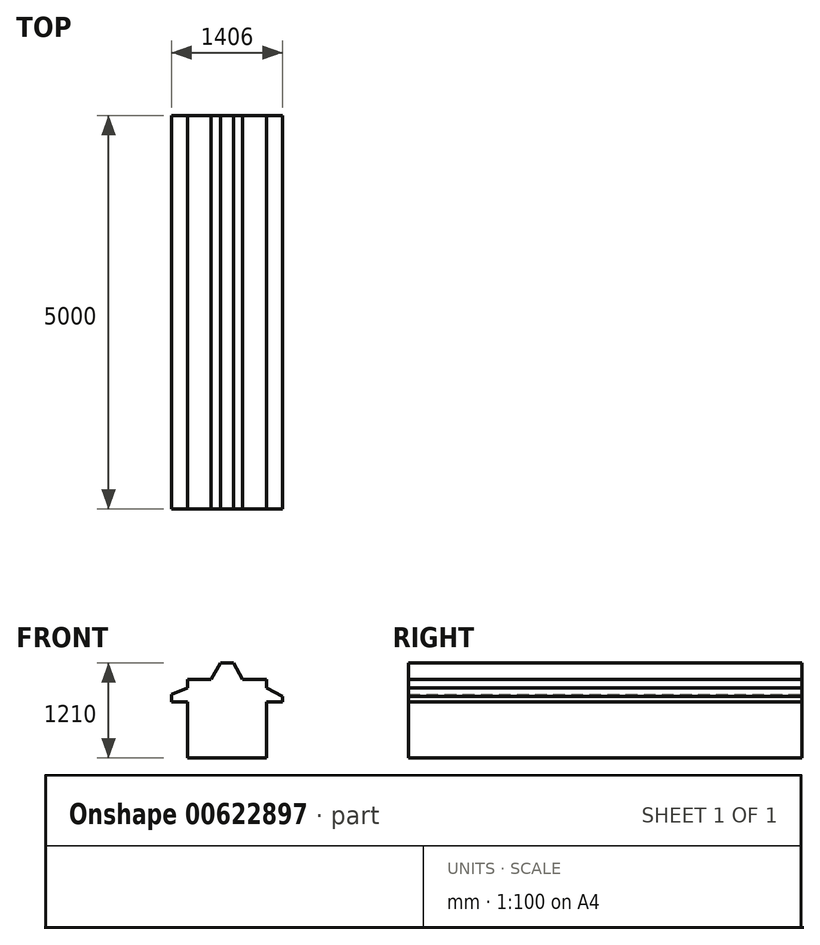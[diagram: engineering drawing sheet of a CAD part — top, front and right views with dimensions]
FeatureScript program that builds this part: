
annotation { "Feature Type Name" : "Feature", "Feature Type Description" : "" }
export const myFeature = defineFeature(function(context is Context, id is Id, definition is map)
    precondition{}
    {
        {
            var Q0;
            Q0=qCreatedBy(makeId("Front.planeOp"),FACE);
            var sketch = newSketch(context, id + "F0", { "sketchPlane" : qUnion([Q0])});
            skLineSegment(sketch, "E0.bottom", {"start": v(0, 0) * mm, "end": v(300, 0) * mm});
            skLineSegment(sketch, "E0.top", {"start": v(0, -1000) * mm, "end": v(1000, -1000) * mm});
            skLineSegment(sketch, "E0.left", {"start": v(0, 0) * mm, "end": v(0, -110) * mm});
            skLineSegment(sketch, "E0.right", {"start": v(1000, 0) * mm, "end": v(1000, -110) * mm});
            skLineSegment(sketch, "E1.top", {"start": v(416.19, 210) * mm, "end": v(583.81, 210) * mm});
            skLineSegment(sketch, "E2", {"start": v(300, 0) * mm, "end": v(416.19, 210) * mm});
            skLineSegment(sketch, "E3", {"start": v(700, 0) * mm, "end": v(583.81, 210) * mm});
            skLineSegment(sketch, "E4", {"start": v(1203, -286) * mm, "end": v(1000, -286) * mm});
            skLineSegment(sketch, "E5", {"start": v(1203, -286) * mm, "end": v(1203, -219.67) * mm});
            skLineSegment(sketch, "E6", {"start": v(1203, -219.67) * mm, "end": v(1000, -110) * mm});
            skLineSegment(sketch, "E7", {"start": v(0, -286) * mm, "end": v(-203, -286) * mm});
            skLineSegment(sketch, "E8", {"start": v(-203, -286) * mm, "end": v(-203, -192.06) * mm});
            skLineSegment(sketch, "E9", {"start": v(-203, -192.06) * mm, "end": v(0, -110) * mm});
            skLineSegment(sketch, "E10.trimOffspring", {"start": v(700, 0) * mm, "end": v(1000, 0) * mm});
            skLineSegment(sketch, "E11.trimOffspring", {"start": v(1000, -286) * mm, "end": v(1000, -1000) * mm});
            skLineSegment(sketch, "E12.trimOffspring", {"start": v(0, -286) * mm, "end": v(0, -1000) * mm});
            skSolve(sketch);
        }
        {
            var Q0;
            Q0 = qSketchRegion(id + "F0", true);
            extrude(context, id + "F1", {"entities" : qUnion([Q0]), "depth" : 5000 * mm, "offsetDistance" : 25 * mm});
        }
    });
